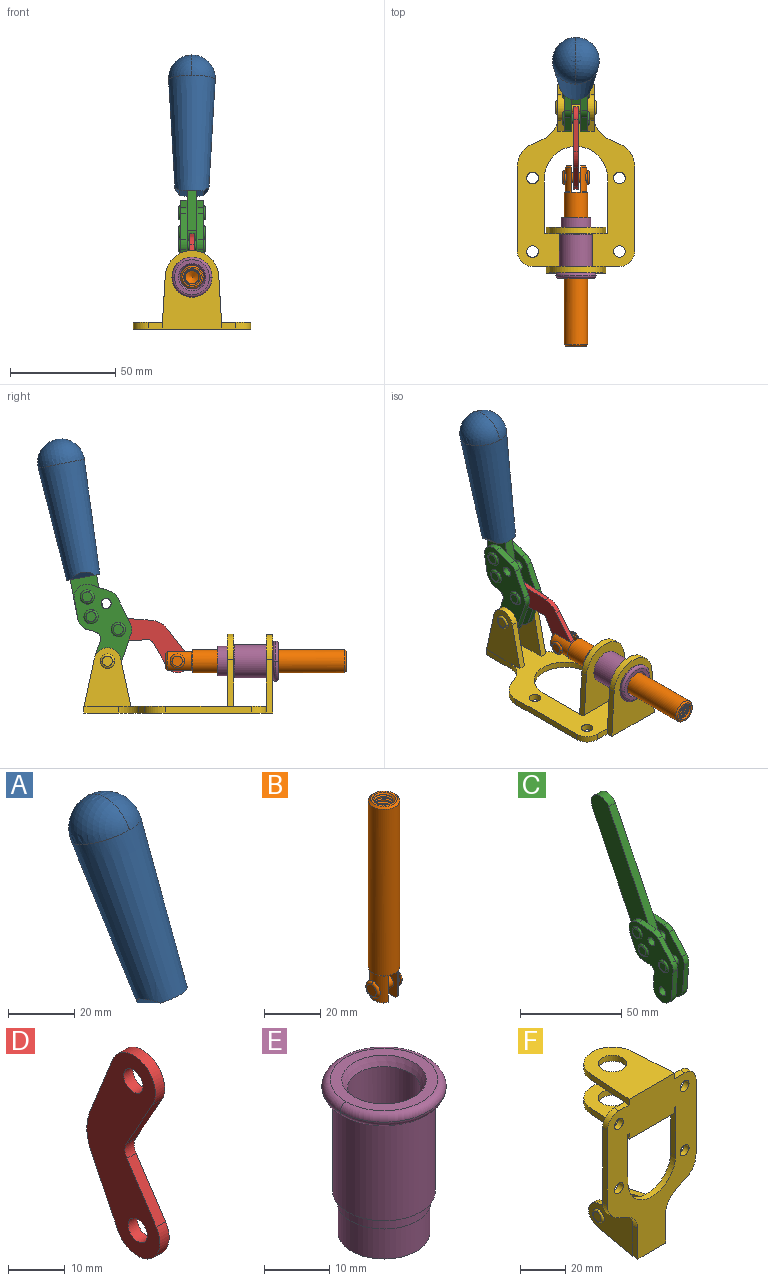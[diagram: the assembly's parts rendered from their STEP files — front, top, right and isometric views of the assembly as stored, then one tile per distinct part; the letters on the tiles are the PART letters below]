
ASSEMBLY  parts=6 mates=6
PART A: 11 faces, bbox 22.3x42.6x64.5 mm
  f0: sphere r=11.13mm, area 411.4mm2, adj f1,f8
  f1: cone r=11.11mm half-angle=3.3deg, axis (0,0.44,0.9), area 3251.8mm2, adj f0,f7,f8,f9,f10
  f2: cylinder r=6.16mm len=11.7mm, axis (1,0,0), area 89.5mm2, adj f3,f4,f5,f6
  f3: plane 60.23x36.75mm, normal (-1,0,0), area 763.6mm2, adj f2,f4,f6,f10
  f4: plane 51.37x25.05mm, normal (0,0.9,-0.44), area 264.2mm2, adj f2,f3,f5,f10
  f5: plane 60.23x36.75mm, normal (1,0,0), area 763.6mm2, adj f2,f4,f6,f10
  f6: plane 51.37x25.05mm, normal (0,-0.9,0.44), area 264.2mm2, adj f2,f3,f5,f10
  f7: plane 9.95x5.95mm, normal (0.71,-0.31,-0.64), area 25.8mm2, adj f1,f10
  f8: sphere r=11.13mm, area 411.4mm2, adj f0,f1
  f9: plane 9.95x5.95mm, normal (-0.71,-0.31,-0.64), area 25.8mm2, adj f1,f10
  f10: plane 14.27x11.38mm, normal (0,-0.44,-0.9), area 106.7mm2, adj f1,f3,f4,f5,f6,f7,f9
PART B: 48 faces, bbox 12.6x11.1x86.1 mm
  f0: torus R=2.41mm, axis (-1,0,0), area 15mm2, adj f30,f32,f34
  f1: torus R=2.41mm, axis (-1,0,0), area 15mm2, adj f29,f31,f33
  f2: cylinder r=5.54mm len=72.39mm, axis (0,0,1), area 2518.5mm2, adj f3,f4,f42,f43
  f3: cone r=5.54mm half-angle=45deg, axis (0,0,1), area 7.6mm2, adj f2,f5,f41
  f4: cone r=5.54mm half-angle=45deg, axis (0,0,-1), area 34.9mm2, adj f2,f39
  f5: cylinder r=5.08mm len=11.48mm, axis (0,0,1), area 108.3mm2, adj f3,f7,f8,f41
  f6: cylinder r=2.41mm len=4.83mm, axis (-1,0,0), area 71.2mm2, adj f40,f41
  f7: cylinder r=2.41mm len=4.83mm, axis (-1,0,0), area 7.6mm2, adj f5,f34
  f8: cone r=5.08mm half-angle=45deg, axis (0,0,1), area 10.6mm2, adj f5,f37,f41
  f9: cone r=3.98mm half-angle=45deg, axis (0,0,1), area 17.6mm2, adj f27,f39,f45,f46,f47
  f10: cylinder r=2.41mm len=4.83mm, axis (-1,0,0), area 7.6mm2, adj f33,f38
  f11: cylinder r=3.2mm len=6.4mm, axis (0,0,1), area 78.4mm2, adj f12,f28,f44,f45,f47
  f12: cylinder r=3.2mm len=6.4mm, axis (0,0,1), area 10.5mm2, adj f11,f13,f45,f47
  f13: cylinder r=3.2mm len=6.4mm, axis (0,0,1), area 10.5mm2, adj f12,f14,f45,f47
  f14: cylinder r=3.2mm len=6.4mm, axis (0,0,1), area 10.5mm2, adj f13,f15,f45,f47
  f15: cylinder r=3.2mm len=6.4mm, axis (0,0,1), area 10.5mm2, adj f14,f16,f45,f47
  f16: cylinder r=3.2mm len=6.4mm, axis (0,0,1), area 10.5mm2, adj f15,f17,f45,f47
  f17: cylinder r=3.2mm len=6.4mm, axis (0,0,1), area 10.5mm2, adj f16,f18,f45,f47
  f18: cylinder r=3.2mm len=6.4mm, axis (0,0,1), area 10.5mm2, adj f17,f19,f45,f47
  f19: cylinder r=3.2mm len=6.4mm, axis (0,0,1), area 10.5mm2, adj f18,f20,f45,f47
  f20: cylinder r=3.2mm len=6.4mm, axis (0,0,1), area 10.5mm2, adj f19,f21,f45,f47
  f21: cylinder r=3.2mm len=6.4mm, axis (0,0,1), area 10.5mm2, adj f20,f22,f45,f47
  f22: cylinder r=3.2mm len=6.4mm, axis (0,0,1), area 10.5mm2, adj f21,f23,f45,f47
  f23: cylinder r=3.2mm len=6.4mm, axis (0,0,1), area 10.5mm2, adj f22,f24,f45,f47
  f24: cylinder r=3.2mm len=6.4mm, axis (0,0,1), area 10.5mm2, adj f23,f25,f45,f47
  f25: cylinder r=3.2mm len=6.4mm, axis (0,0,1), area 10.5mm2, adj f24,f26,f45,f47
  f26: cylinder r=3.2mm len=6.4mm, axis (0,0,1), area 10.5mm2, adj f25,f27,f45,f47
  f27: cylinder r=3.2mm len=6.4mm, axis (0,0,1), area 7.4mm2, adj f9,f26,f45,f47
  f28: cone r=3.2mm half-angle=60deg, axis (0,0,1), area 37.2mm2, adj f11
  f29: plane 4.83x4.83mm, normal (-1,0,0), area 18.3mm2, adj f1,f31
  f30: plane 4.83x4.83mm, normal (1,0,0), area 18.3mm2, adj f0,f32
  f31: torus R=2.41mm, axis (-1,0,0), area 15mm2, adj f1,f29,f33
  f32: torus R=2.41mm, axis (-1,0,0), area 15mm2, adj f0,f30,f34
  f33: plane 6.83x6.83mm, normal (1,0,0), area 18.3mm2, adj f1,f10,f31
  f34: plane 6.83x6.83mm, normal (-1,0,0), area 18.3mm2, adj f0,f7,f32
  f35: cone r=5.08mm half-angle=45deg, axis (0,0,1), area 10.6mm2, adj f36,f38,f40
  f36: plane 7.25x1.97mm, normal (0,0,-1), area 10mm2, adj f35,f40
  f37: plane 7.25x1.97mm, normal (0,0,-1), area 10mm2, adj f8,f41
  f38: cylinder r=5.08mm len=11.48mm, axis (0,0,1), area 108.3mm2, adj f10,f35,f40,f42
  f39: plane 9.55x9.55mm, normal (0,0,1), area 22mm2, adj f4,f9
  f40: plane 12.76x10.09mm, normal (1,0,0), area 95.7mm2, adj f6,f35,f36,f38,f42,f43
  f41: plane 12.76x10.09mm, normal (-1,0,0), area 95.7mm2, adj f3,f5,f6,f8,f37,f43
  f42: cone r=5.54mm half-angle=45deg, axis (0,0,1), area 7.6mm2, adj f2,f38,f40
  f43: plane 11.07x4.7mm, normal (0,0,-1), area 50.4mm2, adj f2,f40,f41
  f44: plane 0.89x0.62mm, normal (-1,0,0), area 0.3mm2, adj f11,f45,f46,f47
  f45: bspline ~24.8x7.63mm, area 266.6mm2, adj f9,f11,f12,f13,f14,f15,f16,f17
  f46: bspline ~24.87x7.63mm, area 73.6mm2, adj f9,f44,f45,f47
  f47: bspline ~24.98x7.63mm, area 272.5mm2, adj f9,f11,f12,f13,f14,f15,f16,f17
PART C: 59 faces, bbox 12.9x60.2x99.6 mm
  f0: torus R=2.39mm, axis (-1,0,0), area 14.9mm2, adj f20,f43,f51
  f1: torus R=2.39mm, axis (-1,0,0), area 14.9mm2, adj f19,f42,f51
  f2: torus R=2.39mm, axis (-1,0,0), area 14.9mm2, adj f18,f35,f51
  f3: torus R=2.39mm, axis (-1,0,0), area 14.9mm2, adj f14,f17,f23
  f4: torus R=2.39mm, axis (-1,0,0), area 14.9mm2, adj f13,f16,f23
  f5: torus R=2.39mm, axis (-1,0,0), area 14.9mm2, adj f12,f15,f23
  f6: cylinder r=2.39mm len=4.78mm, axis (1,0,0), area 46.5mm2, adj f48,f50,f51
  f7: cylinder r=2.39mm len=4.78mm, axis (1,0,0), area 46.5mm2, adj f50,f51
  f8: cylinder r=6.35mm len=12.68mm, axis (1,0,0), area 61.8mm2, adj f38,f39,f50,f51
  f9: cylinder r=2.39mm len=4.78mm, axis (-1,0,0), area 70.5mm2, adj f46,f50
  f10: cylinder r=2.39mm len=4.78mm, axis (-1,0,0), area 46.5mm2, adj f23,f45,f46
  f11: cylinder r=2.39mm len=4.78mm, axis (-1,0,0), area 46.5mm2, adj f23,f46
  f12: plane 4.78x4.78mm, normal (1,0,0), area 17.9mm2, adj f5,f15
  f13: plane 4.78x4.78mm, normal (1,0,0), area 17.9mm2, adj f4,f16
  f14: plane 4.78x4.78mm, normal (1,0,0), area 17.9mm2, adj f3,f17
  f15: torus R=2.39mm, axis (-1,0,0), area 14.9mm2, adj f5,f12,f23
  f16: torus R=2.39mm, axis (-1,0,0), area 14.9mm2, adj f4,f13,f23
  f17: torus R=2.39mm, axis (-1,0,0), area 14.9mm2, adj f3,f14,f23
  f18: plane 4.78x4.78mm, normal (-1,0,0), area 17.9mm2, adj f2,f35
  f19: plane 4.78x4.78mm, normal (-1,0,0), area 17.9mm2, adj f1,f42
  f20: plane 4.78x4.78mm, normal (-1,0,0), area 17.9mm2, adj f0,f43
  f21: plane 2.26x0.2mm, normal (1,0,0), area 0.2mm2, adj f31,f44
  f22: plane 2.26x0.2mm, normal (-1,0,0), area 0.2mm2, adj f41,f44
  f23: plane 39.37x30.77mm, normal (1,0,0), area 565.5mm2, adj f3,f4,f5,f10,f11,f15,f16,f17
  f24: cylinder r=6.1mm len=4.15mm, axis (-1,0,0), area 14.7mm2, adj f23,f25,f32,f46
  f25: plane 10.25x9.01mm, normal (0,-0.75,0.66), area 42.3mm2, adj f23,f24,f26,f46
  f26: cylinder r=6.35mm len=4.64mm, axis (-1,0,0), area 15.6mm2, adj f23,f25,f27,f46
  f27: plane 15.84x3.1mm, normal (0,-1,-0.07), area 49.2mm2, adj f23,f26,f28,f46
  f28: cylinder r=6.35mm len=12.68mm, axis (-1,0,0), area 61.8mm2, adj f23,f27,f29,f46
  f29: plane 8.11x3.1mm, normal (0,1,0.07), area 25.2mm2, adj f23,f28,f30,f46
  f30: cylinder r=3.05mm len=3.25mm, axis (-1,0,0), area 14.8mm2, adj f23,f29,f31,f46
  f31: plane 5.99x3.1mm, normal (0,0.07,-1), area 18.6mm2, adj f21,f23,f30,f44,f46
  f32: plane 9.5x3.1mm, normal (0,-0.07,1), area 29.5mm2, adj f23,f24,f33,f46,f47
  f33: cylinder r=6.1mm len=8.63mm, axis (-1,0,0), area 39.1mm2, adj f23,f32,f34,f47
  f34: plane 8.65x3.96mm, normal (0,0.91,-0.42), area 29.5mm2, adj f23,f33,f44,f47
  f35: torus R=2.39mm, axis (-1,0,0), area 14.9mm2, adj f2,f18,f51
  f36: plane 10.25x9.01mm, normal (0,-0.75,0.66), area 42.3mm2, adj f37,f49,f50,f51
  f37: cylinder r=6.35mm len=4.64mm, axis (1,0,0), area 15.6mm2, adj f36,f38,f50,f51
  f38: plane 15.84x3.1mm, normal (0,-1,-0.07), area 49.2mm2, adj f8,f37,f50,f51
  f39: plane 8.11x3.1mm, normal (0,1,0.07), area 25.2mm2, adj f8,f40,f50,f51
  f40: cylinder r=3.05mm len=3.25mm, axis (1,0,0), area 14.8mm2, adj f39,f41,f50,f51
  f41: plane 5.99x3.1mm, normal (0,0.07,-1), area 18.6mm2, adj f22,f40,f44,f50,f51
  f42: torus R=2.39mm, axis (-1,0,0), area 14.9mm2, adj f1,f19,f51
  f43: torus R=2.39mm, axis (-1,0,0), area 14.9mm2, adj f0,f20,f51
  f44: cylinder r=6.35mm len=12.12mm, axis (-1,0,0), area 128.9mm2, adj f21,f22,f23,f31,f34,f41,f46,f47
  f45: plane 2.65x1.35mm, normal (1,0,0), area 1mm2, adj f10,f55
  f46: plane 39.08x20.42mm, normal (-1,0,0), area 412.5mm2, adj f9,f10,f11,f24,f25,f26,f27,f28
  f47: plane 77.62x39.82mm, normal (1,0,0), area 850mm2, adj f32,f33,f34,f44,f53,f54,f55
  f48: plane 2.65x1.35mm, normal (-1,0,0), area 1mm2, adj f6,f55
  f49: cylinder r=6.1mm len=4.15mm, axis (1,0,0), area 14.7mm2, adj f36,f50,f51,f56
  f50: plane 39.08x20.42mm, normal (1,0,0), area 412.5mm2, adj f6,f7,f8,f9,f36,f37,f38,f39
  f51: plane 39.37x30.77mm, normal (-1,0,0), area 565.5mm2, adj f0,f1,f2,f6,f7,f8,f35,f36
  f52: plane 8.65x3.96mm, normal (0,0.91,-0.42), area 29.5mm2, adj f44,f51,f57,f58
  f53: plane 68.49x33.4mm, normal (0,0.9,-0.44), area 358.1mm2, adj f44,f47,f54,f58
  f54: cylinder r=6.35mm len=12.06mm, axis (1,0,0), area 93.7mm2, adj f47,f53,f55,f58
  f55: plane 68.49x33.4mm, normal (0,-0.9,0.44), area 358.1mm2, adj f44,f45,f46,f47,f48,f50,f54,f58
  f56: plane 9.5x3.1mm, normal (0,-0.07,1), area 29.5mm2, adj f49,f50,f51,f57,f58
  f57: cylinder r=6.1mm len=8.63mm, axis (1,0,0), area 39.1mm2, adj f51,f52,f56,f58
  f58: plane 77.62x39.82mm, normal (-1,0,0), area 850mm2, adj f44,f52,f53,f54,f55,f56,f57
PART D: 12 faces, bbox 2.3x18.2x42.8 mm
  f0: cylinder r=2.4mm len=4.8mm, axis (1,0,0), area 34.9mm2, adj f4,f11
  f1: cylinder r=10.41mm len=8.47mm, axis (1,0,0), area 20.2mm2, adj f4,f9,f10,f11
  f2: cylinder r=3.05mm len=3.16mm, axis (1,0,0), area 7.7mm2, adj f4,f6,f7,f11
  f3: cylinder r=2.4mm len=4.8mm, axis (1,0,0), area 34.9mm2, adj f4,f11
  f4: plane 42.81x18.23mm, normal (-1,0,0), area 414.1mm2, adj f0,f1,f2,f3,f5,f6,f7,f8
  f5: cylinder r=5.54mm len=10.67mm, axis (1,0,0), area 41.8mm2, adj f4,f6,f10,f11
  f6: plane 11.66x6.53mm, normal (0,-0.87,-0.49), area 30.9mm2, adj f2,f4,f5,f11
  f7: plane 11.17x7.33mm, normal (0,-0.84,0.55), area 30.9mm2, adj f2,f4,f8,f11
  f8: cylinder r=5.54mm len=10.51mm, axis (1,0,0), area 41.8mm2, adj f4,f7,f9,f11
  f9: plane 13.67x6.67mm, normal (0,0.9,-0.44), area 35.1mm2, adj f1,f4,f8,f11
  f10: plane 14.1x5.7mm, normal (0,0.93,0.37), area 35.1mm2, adj f1,f4,f5,f11
  f11: plane 42.81x18.23mm, normal (1,0,0), area 414.1mm2, adj f0,f1,f2,f3,f5,f6,f7,f8
PART E: 15 faces, bbox 20.6x20.6x28.7 mm
  f0: torus R=8.26mm, axis (0,0,1), area 56.8mm2, adj f1,f10,f12
  f1: torus R=8.26mm, axis (0,0,1), area 56.8mm2, adj f0,f6,f13
  f2: cylinder r=5.59mm len=25.91mm, axis (0,0,1), area 909.6mm2, adj f3,f4
  f3: cone r=6.86mm half-angle=45deg, axis (0,0,-1), area 70.2mm2, adj f2,f14
  f4: cone r=6.47mm half-angle=30deg, axis (0,0,1), area 66.7mm2, adj f2,f13
  f5: cylinder r=7.04mm len=14.07mm, axis (0,0,1), area 252.6mm2, adj f11,f14
  f6: torus R=8.26mm, axis (0,0,1), area 56.8mm2, adj f1,f12,f13
  f7: cylinder r=7.16mm len=14.33mm, axis (0,0,1), area 91.5mm2, adj f9,f11
  f8: cylinder r=7.86mm len=18.42mm, axis (0,0,1), area 909.6mm2, adj f9,f10
  f9: plane 15.72x15.72mm, normal (0,0,-1), area 33mm2, adj f7,f8
  f10: plane 16.51x16.51mm, normal (0,0,-1), area 19.9mm2, adj f0,f8,f12
  f11: plane 14.33x14.33mm, normal (0,0,-1), area 5.7mm2, adj f5,f7
  f12: torus R=8.26mm, axis (0,0,1), area 56.8mm2, adj f0,f6,f10
  f13: plane 16.51x16.51mm, normal (0,0,1), area 82.7mm2, adj f1,f4,f6
  f14: plane 14.07x14.07mm, normal (0,0,-1), area 7.8mm2, adj f3,f5
PART F: 55 faces, bbox 55.7x37.4x89.8 mm
  f0: torus R=2.41mm, axis (-1,0,0), area 15mm2, adj f11,f15,f25
  f1: torus R=2.41mm, axis (-1,0,0), area 15mm2, adj f10,f12,f22
  f2: cylinder r=2.78mm len=5.56mm, axis (0,-1,0), area 54.2mm2, adj f30,f54
  f3: cylinder r=14.99mm len=29.97mm, axis (0,-1,0), area 145.9mm2, adj f30,f49,f53,f54
  f4: cylinder r=2.78mm len=5.56mm, axis (0,-1,0), area 54.2mm2, adj f30,f54
  f5: cylinder r=2.78mm len=5.56mm, axis (0,-1,0), area 54.2mm2, adj f30,f54
  f6: cylinder r=2.78mm len=5.56mm, axis (0,-1,0), area 54.2mm2, adj f30,f54
  f7: cylinder r=6.35mm len=12.7mm, axis (0,0,1), area 123.6mm2, adj f27,f51
  f8: cylinder r=6.35mm len=12.7mm, axis (0,0,-1), area 124.7mm2, adj f21,f35
  f9: cylinder r=2.41mm len=11.18mm, axis (-1,0,0), area 169.4mm2, adj f16,f19
  f10: plane 4.83x4.83mm, normal (1,0,0), area 18.3mm2, adj f1,f12
  f11: plane 4.83x4.83mm, normal (-1,0,0), area 18.3mm2, adj f0,f15
  f12: torus R=2.41mm, axis (-1,0,0), area 15mm2, adj f1,f10,f22
  f13: cylinder r=6.35mm len=12.41mm, axis (1,0,0), area 53.4mm2, adj f18,f19,f22,f23
  f14: cylinder r=6.35mm len=12.41mm, axis (-1,0,0), area 53.4mm2, adj f16,f17,f24,f25
  f15: torus R=2.41mm, axis (-1,0,0), area 15mm2, adj f0,f11,f25
  f16: plane 27.86x22.35mm, normal (1,0,0), area 425.4mm2, adj f9,f14,f17,f24,f30
  f17: plane 22.86x4.97mm, normal (0,0.21,0.98), area 72.5mm2, adj f14,f16,f25,f30
  f18: plane 22.86x4.97mm, normal (0,0.21,0.98), area 72.5mm2, adj f13,f19,f22,f30
  f19: plane 27.86x22.35mm, normal (-1,0,0), area 425.4mm2, adj f9,f13,f18,f23,f30
  f20: cylinder r=12.7mm len=25.35mm, axis (0,0,-1), area 119.8mm2, adj f21,f34,f35,f36
  f21: plane 34.21x28.07mm, normal (0,0,-1), area 702.4mm2, adj f8,f20,f30,f34,f36
  f22: plane 27.96x22.45mm, normal (1,0,0), area 407.2mm2, adj f1,f12,f13,f18,f23,f30,f42,f43
  f23: plane 22.86x4.97mm, normal (0,0.21,-0.98), area 72.5mm2, adj f13,f19,f22,f44
  f24: plane 22.86x4.97mm, normal (0,0.21,-0.98), area 72.5mm2, adj f14,f16,f25,f44
  f25: plane 27.86x22.35mm, normal (-1,0,0), area 407.1mm2, adj f0,f14,f15,f17,f24,f30,f45,f46
  f26: plane 3.1x0.95mm, normal (0,0,-1), area 2.7mm2, adj f30,f49,f50,f54
  f27: plane 34.21x28.07mm, normal (0,0,1), area 702.4mm2, adj f7,f28,f30,f50,f52
  f28: cylinder r=12.7mm len=25.35mm, axis (0,0,1), area 118.8mm2, adj f27,f50,f51,f52
  f29: plane 3.1x0.95mm, normal (0,0,-1), area 2.7mm2, adj f30,f52,f53,f54
  f30: plane 86.54x55.63mm, normal (0,1,0), area 2362.9mm2, adj f2,f3,f4,f5,f6,f16,f17,f18
  f31: plane 40.56x3.1mm, normal (-1,0,0), area 125.7mm2, adj f30,f32,f48,f54
  f32: cylinder r=7.11mm len=7.11mm, axis (0,-1,0), area 34.6mm2, adj f30,f31,f33,f54
  f33: plane 6.67x3.1mm, normal (0,0,1), area 20.4mm2, adj f30,f32,f34,f54
  f34: plane 25.39x3.13mm, normal (-1,0.06,0), area 79.5mm2, adj f20,f21,f33,f35,f54
  f35: plane 37.31x28.45mm, normal (0,0,1), area 789.9mm2, adj f8,f20,f34,f36,f54
  f36: plane 25.39x3.13mm, normal (1,0.06,0), area 79.5mm2, adj f20,f21,f35,f37,f54
  f37: plane 6.67x3.1mm, normal (0,0,1), area 20.4mm2, adj f30,f36,f38,f54
  f38: cylinder r=7.11mm len=7.11mm, axis (0,-1,0), area 34.6mm2, adj f30,f37,f39,f54
  f39: plane 40.56x3.1mm, normal (1,0,0), area 125.7mm2, adj f30,f38,f40,f54
  f40: cylinder r=11.18mm len=10.16mm, axis (0,-1,0), area 39.5mm2, adj f30,f39,f41,f54
  f41: plane 6.09x3.1mm, normal (0.42,0,-0.91), area 20.8mm2, adj f30,f40,f42,f54
  f42: cylinder r=11.18mm len=9.41mm, axis (0,-1,0), area 37.2mm2, adj f22,f30,f41,f43,f54
  f43: plane 16.5x3.1mm, normal (1,0,0), area 51.1mm2, adj f22,f42,f44,f54
  f44: plane 17.37x3.1mm, normal (0,0,-1), area 53.8mm2, adj f23,f24,f30,f43,f45,f54
  f45: plane 16.5x3.1mm, normal (-1,0,0), area 51.1mm2, adj f25,f44,f46,f54
  f46: cylinder r=11.18mm len=9.41mm, axis (0,-1,0), area 37.2mm2, adj f25,f30,f45,f47,f54
  f47: plane 6.09x3.1mm, normal (-0.42,0,-0.91), area 20.8mm2, adj f30,f46,f48,f54
  f48: cylinder r=11.18mm len=10.16mm, axis (0,-1,0), area 39.5mm2, adj f30,f31,f47,f54
  f49: plane 26.54x3.1mm, normal (-1,0,0), area 82.3mm2, adj f3,f26,f30,f54
  f50: plane 25.39x3.1mm, normal (1,0.06,0), area 78.8mm2, adj f26,f27,f28,f51,f54
  f51: plane 37.31x28.45mm, normal (0,0,-1), area 789.9mm2, adj f7,f28,f50,f52,f54
  f52: plane 25.39x3.1mm, normal (-1,0.06,0), area 78.8mm2, adj f27,f28,f29,f51,f54
  f53: plane 26.54x3.1mm, normal (1,0,0), area 82.3mm2, adj f3,f29,f30,f54
  f54: plane 89.66x55.63mm, normal (0,-1,0), area 2678.5mm2, adj f2,f3,f4,f5,f6,f26,f29,f31
PLACE A rot(axis=(1,0,0),15deg) t=(-0.04,9.15,49.24)mm
PLACE B rot(axis=(1,0,0),90deg) t=(0,23.56,0)mm
PLACE C rot(axis=(1,0,0),15deg) t=(0,9.15,49.24)mm
PLACE D rot(axis=(1,0,0),120.2deg) t=(0,33.84,11.13)mm
PLACE E rot(axis=(1,0,0),90deg) t=(0,9.14,0)mm
PLACE F rot(axis=(1,0,0),90deg) t=(0,9.14,0)mm fixed
MATE revolute C.f4 <-> D.f3  axis (-1,0,0) through (0,36.06,39.62)mm
MATE revolute D.f5 <-> B.f6  axis (1,0,0) through (0,8.09,24.61)mm
MATE fastened A.f2 <-> C.f54  axis (1,0,0) through (-2.35,63.6,120.54)mm
MATE revolute C.f7 <-> F.f0  axis (1,0,0) through (0,41.23,24.61)mm
MATE fastened E.f2 <-> F.f7  axis (0,-1,0) through (0,-37.25,24.61)mm
MATE slider B.f2 <-> E.f2  axis (0,-1,0) through (0,-35.22,24.61)mm
